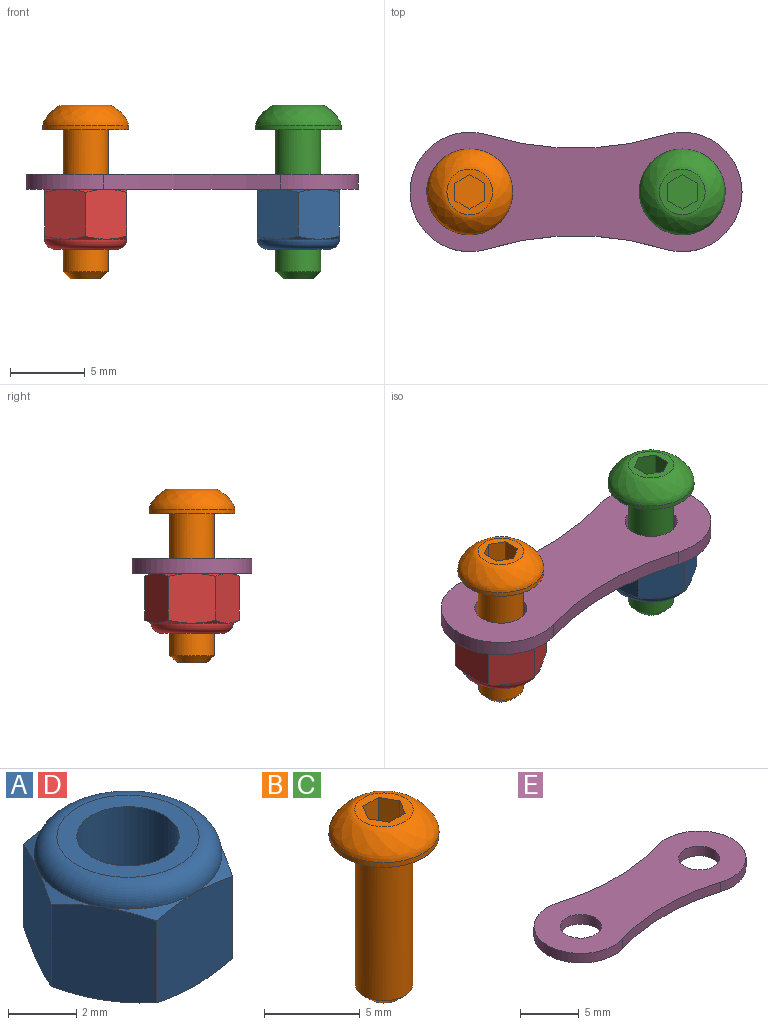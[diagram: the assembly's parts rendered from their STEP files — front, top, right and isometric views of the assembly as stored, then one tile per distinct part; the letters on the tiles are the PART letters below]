
ASSEMBLY  parts=5 mates=4
PART A: 22 faces, bbox 6.6x6.6x4.2 mm
  f0: plane 3.59x2.99mm, normal (-0.87,0.5,0), area 10.2mm2, adj f1,f5,f7,f9,f13,f14,f16,f21
  f1: plane 3.59x2.99mm, normal (-0.87,-0.5,0), area 10.2mm2, adj f0,f2,f7,f9,f10,f14,f20,f21
  f2: plane 3.6x3.42mm, normal (0,-1,0), area 10.2mm2, adj f1,f3,f7,f10,f11,f14,f19,f20
  f3: plane 3.59x2.99mm, normal (0.87,-0.5,0), area 10.2mm2, adj f2,f4,f7,f11,f12,f14,f18,f19
  f4: plane 3.59x2.99mm, normal (0.87,0.5,0), area 10.2mm2, adj f3,f5,f7,f12,f14,f15,f17,f18
  f5: plane 3.6x3.42mm, normal (0,1,0), area 10.2mm2, adj f0,f4,f7,f13,f14,f15,f16,f17
  f6: plane 4.17x4.17mm, normal (0,0,1), area 6.6mm2, adj f8,f14
  f7: plane 5.5x5.5mm, normal (0,0,-1), area 16.7mm2, adj f0,f1,f2,f3,f4,f5,f8,f16
  f8: cylinder r=1.5mm len=4mm, axis (0,0,1), area 37.7mm2, adj f6,f7
  f9: cone r=3.18mm half-angle=65deg, axis (0,0,-1), area 0.7mm2, adj f0,f1,f14
  f10: cone r=3.18mm half-angle=65deg, axis (0,0,-1), area 0.7mm2, adj f1,f2,f14
  f11: cone r=3.18mm half-angle=65deg, axis (0,0,-1), area 0.7mm2, adj f2,f3,f14
  f12: cone r=3.18mm half-angle=65deg, axis (0,0,-1), area 0.7mm2, adj f3,f4,f14
  f13: cone r=3.18mm half-angle=65deg, axis (0,0,-1), area 0.7mm2, adj f0,f5,f14
  f14: torus R=2.08mm, axis (0,0,-1), area 16.5mm2, adj f0,f1,f2,f3,f4,f5,f6,f9
  f15: cone r=3.18mm half-angle=65deg, axis (0,0,-1), area 0.7mm2, adj f4,f5,f14
  f16: cone r=2.75mm half-angle=65deg, axis (0,0,1), area 0.7mm2, adj f0,f5,f7
  f17: cone r=2.75mm half-angle=65deg, axis (0,0,1), area 0.7mm2, adj f4,f5,f7
  f18: cone r=2.75mm half-angle=65deg, axis (0,0,1), area 0.7mm2, adj f3,f4,f7
  f19: cone r=2.75mm half-angle=65deg, axis (0,0,1), area 0.7mm2, adj f2,f3,f7
  f20: cone r=2.75mm half-angle=65deg, axis (0,0,1), area 0.7mm2, adj f1,f2,f7
  f21: cone r=2.75mm half-angle=65deg, axis (0,0,1), area 0.7mm2, adj f0,f1,f7
PART B: 14 faces, bbox 5.8x5.8x11.7 mm
  f0: plane 3.07x3.07mm, normal (0,0,1), area 3.9mm2, adj f3,f4,f5,f6,f7,f8,f10
  f1: cylinder r=2.88mm len=5.75mm, axis (0,0,-1), area 5.4mm2, adj f2,f10
  f2: plane 5.75x5.75mm, normal (0,0,-1), area 18.9mm2, adj f1,f11
  f3: plane 1.5x1mm, normal (-0.87,-0.5,0), area 1.7mm2, adj f0,f4,f8,f9
  f4: plane 1.5x1.15mm, normal (0,-1,0), area 1.7mm2, adj f0,f3,f5,f9
  f5: plane 1.5x1mm, normal (0.87,-0.5,0), area 1.7mm2, adj f0,f4,f6,f9
  f6: plane 1.5x1mm, normal (0.87,0.5,0), area 1.7mm2, adj f0,f5,f7,f9
  f7: plane 1.5x1.15mm, normal (0,1,0), area 1.7mm2, adj f0,f6,f8,f9
  f8: plane 1.5x1mm, normal (-0.87,0.5,0), area 1.7mm2, adj f0,f3,f7,f9
  f9: plane 2.31x2mm, normal (0,0,1), area 3.5mm2, adj f3,f4,f5,f6,f7,f8
  f10: bspline ~5.75x5.75mm, area 29.2mm2, adj f0,f1
  f11: cylinder r=1.5mm len=9.5mm, axis (0,0,1), area 89.5mm2, adj f2,f13
  f12: plane 2x2mm, normal (0,0,-1), area 3.1mm2, adj f13
  f13: cone r=1mm half-angle=45deg, axis (0,0,1), area 5.6mm2, adj f11,f12
PART C: same geometry as B
PART D: same geometry as A
PART E: 8 faces, bbox 22.2x8x1 mm
  f0: cylinder r=20mm len=11.86mm, axis (0,0,-1), area 12mm2, adj f1,f5,f6,f7
  f1: cylinder r=4mm len=8mm, axis (0,0,-1), area 15mm2, adj f0,f2,f6,f7
  f2: cylinder r=20mm len=11.86mm, axis (0,0,-1), area 12mm2, adj f1,f5,f6,f7
  f3: cylinder r=1.75mm len=3.5mm, axis (0,0,-1), area 11mm2, adj f6,f7
  f4: cylinder r=1.75mm len=3.5mm, axis (0,0,-1), area 11mm2, adj f6,f7
  f5: cylinder r=4mm len=8mm, axis (0,0,-1), area 15mm2, adj f0,f2,f6,f7
  f6: plane 22.24x8mm, normal (0,0,1), area 126.1mm2, adj f0,f1,f2,f3,f4,f5
  f7: plane 22.24x8mm, normal (0,0,-1), area 126.1mm2, adj f0,f1,f2,f3,f4,f5
PLACE A rot(axis=(0.71,0.71,0),180deg) t=(-14.45,7.27,5.65)mm
PLACE B rot(axis=(0,0,1),90deg) t=(-28.68,7.27,9.65)mm
PLACE C rot(axis=(0,0,1),90deg) t=(-14.45,7.27,9.65)mm
PLACE D rot(axis=(0.71,0.71,0),180deg) t=(-28.68,7.27,5.65)mm
PLACE E rot(axis=(1,0,0),180deg) t=(-21.57,7.27,6.65)mm
MATE fastened A.f8 <-> C.f1  axis (0,0,-1) through (-14.45,7.27,5.65)mm
MATE fastened E.f3 <-> B.f1  axis (0,0,1) through (-28.68,7.27,6.65)mm
MATE fastened E.f1 <-> C.f1  axis (0,0,1) through (-14.45,7.27,6.65)mm
MATE fastened D.f8 <-> B.f1  axis (0,0,-1) through (-28.68,7.27,5.65)mm
